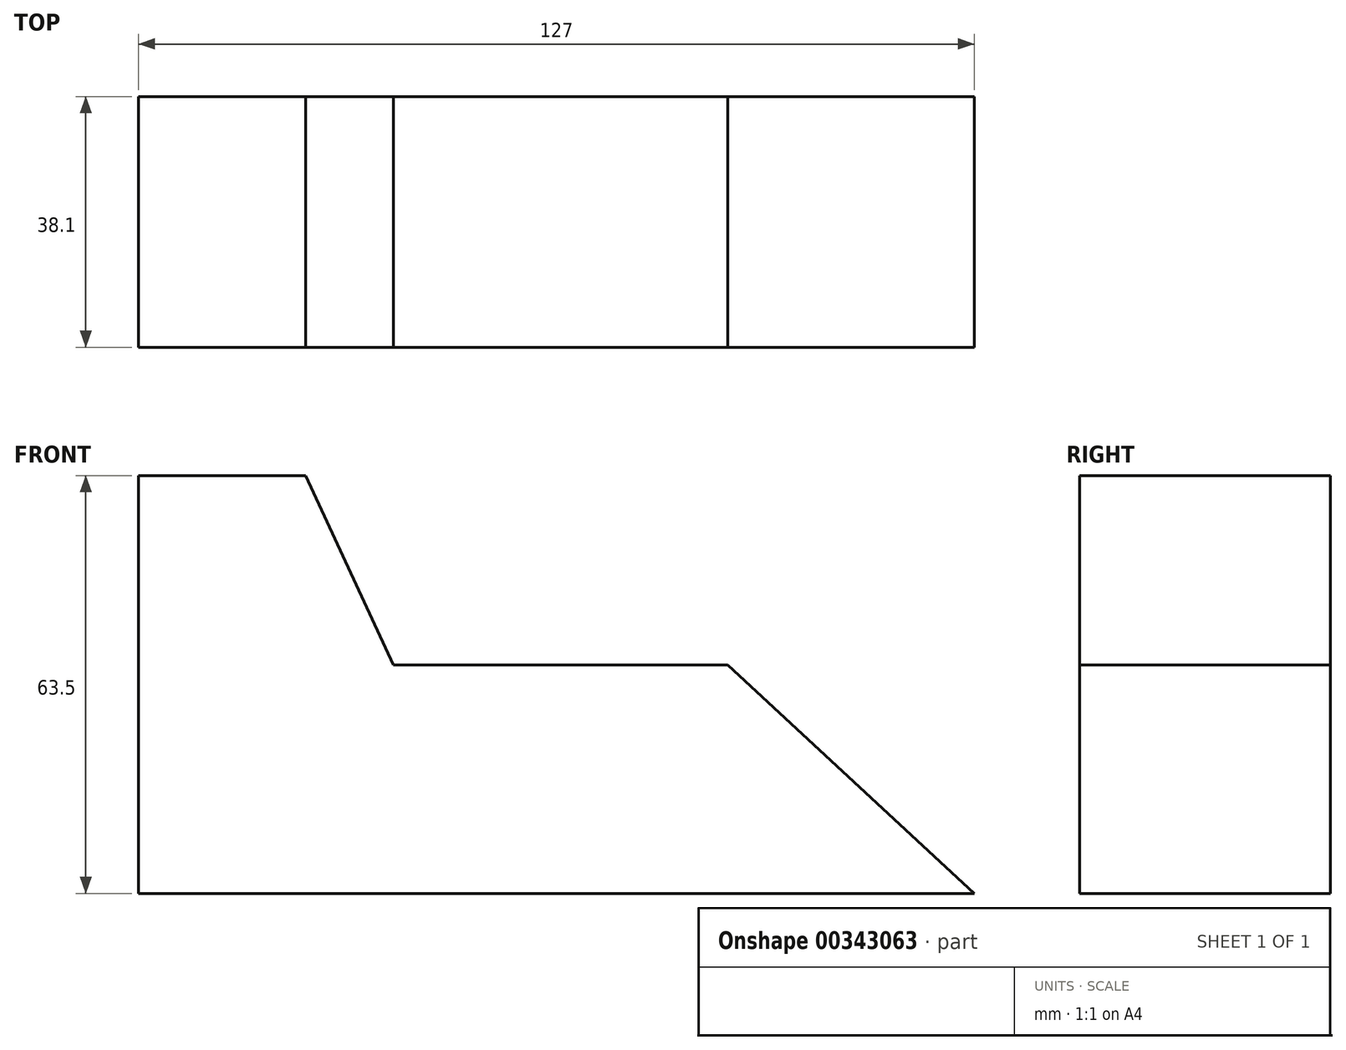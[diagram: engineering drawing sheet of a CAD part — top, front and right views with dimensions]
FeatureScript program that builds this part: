
annotation { "Feature Type Name" : "Feature", "Feature Type Description" : "" }
export const myFeature = defineFeature(function(context is Context, id is Id, definition is map)
    precondition{}
    {
        {
            var Q0;
            Q0=qCreatedBy(makeId("Front.planeOp"),FACE);
            var sketch = newSketch(context, id + "F0", { "sketchPlane" : qUnion([Q0])});
            skLineSegment(sketch, "E0", {"start": v(-50.43, -44.16) * mm, "end": v(76.57, -44.16) * mm});
            skLineSegment(sketch, "E1", {"start": v(-50.43, -44.16) * mm, "end": v(-50.43, 19.34) * mm});
            skLineSegment(sketch, "E2", {"start": v(-50.43, 19.34) * mm, "end": v(-25.03, 19.34) * mm});
            skLineSegment(sketch, "E3", {"start": v(-25.03, 19.34) * mm, "end": v(-11.7, -9.48) * mm});
            skLineSegment(sketch, "E4", {"start": v(-11.7, -9.48) * mm, "end": v(39.1, -9.48) * mm});
            skLineSegment(sketch, "E5", {"start": v(39.1, -9.48) * mm, "end": v(76.57, -44.16) * mm});
            skSolve(sketch);
        }
        {
            var Q0;
            Q0 = qSketchRegion(id + "F0", true);
            extrude(context, id + "F1", {"entities" : qUnion([Q0]), "depth" : 38.1 * mm});
        }
    });
